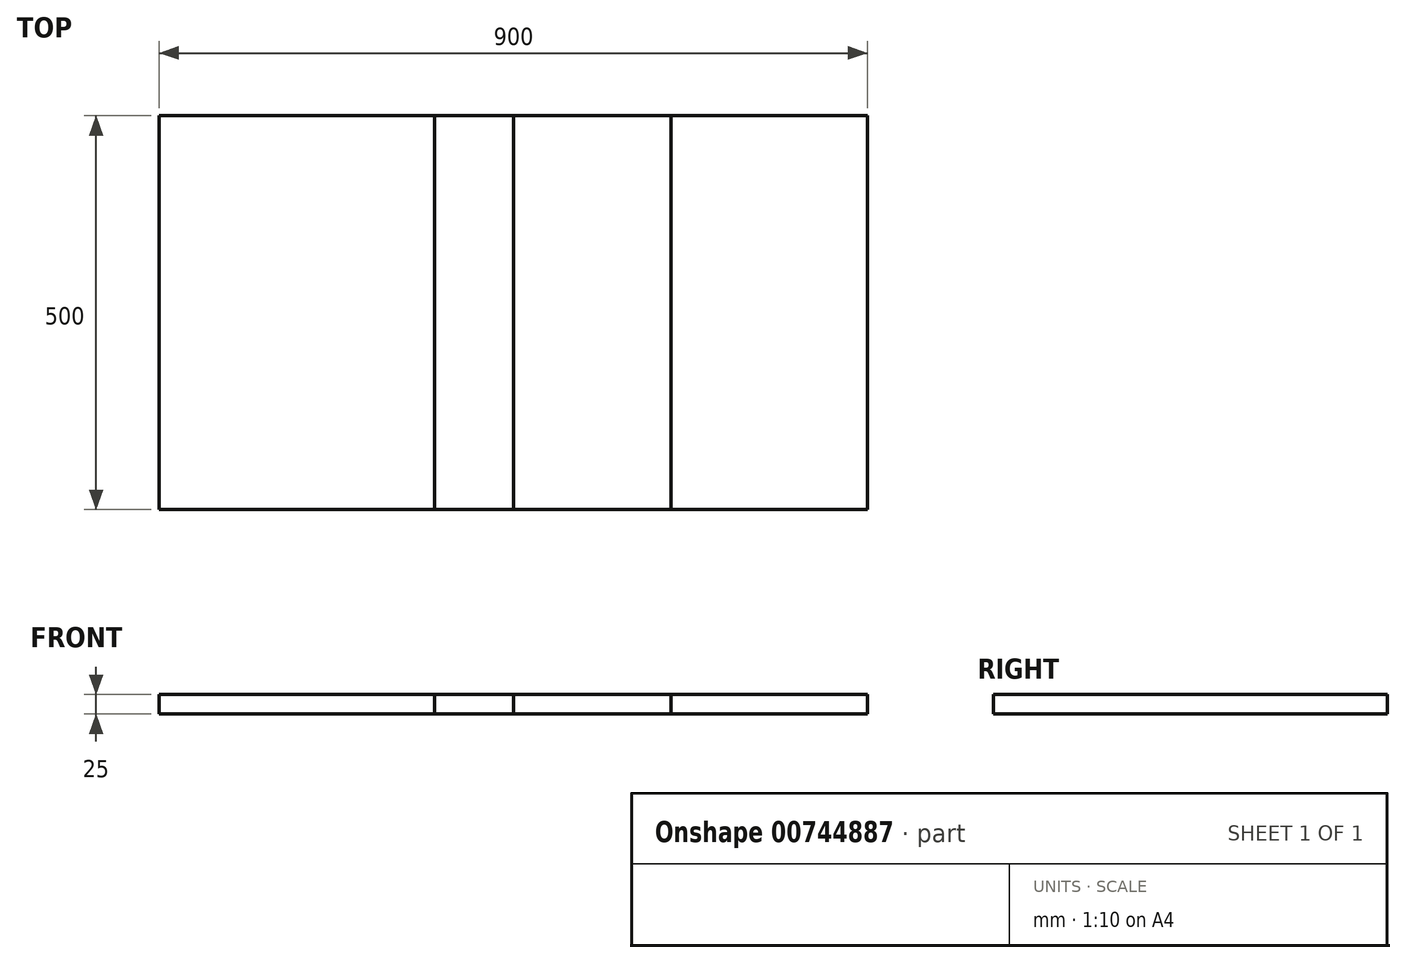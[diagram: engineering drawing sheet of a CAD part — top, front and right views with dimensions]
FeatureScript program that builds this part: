
annotation { "Feature Type Name" : "Feature", "Feature Type Description" : "" }
export const myFeature = defineFeature(function(context is Context, id is Id, definition is map)
    precondition{}
    {
        {
            var Q0;
            Q0=qCreatedBy(makeId("Top.planeOp"),FACE);
            var sketch = newSketch(context, id + "F0", { "sketchPlane" : qUnion([Q0])});
            skLineSegment(sketch, "E0.bottom", {"start": v(-175, 250) * mm, "end": v(175, 250) * mm});
            skLineSegment(sketch, "E0.top", {"start": v(-175, -250) * mm, "end": v(175, -250) * mm});
            skLineSegment(sketch, "E0.left", {"start": v(-175, 250) * mm, "end": v(-175, -250) * mm});
            skLineSegment(sketch, "E0.right", {"start": v(175, 250) * mm, "end": v(175, -250) * mm});
            skPoint(sketch, "E0.middle", {"position": v(0, 0) * mm});
            skSolve(sketch);
        }
        {
            var Q0;
            Q0 = qSketchRegion(id + "F0", true);
            extrude(context, id + "F1", {"entities" : qUnion([Q0]), "depth" : 25 * mm, "offsetDistance" : 25 * mm});
        }
        {
            var Q0;
            Q0=makeQuery(id+"F1.opExtrude","CAP_FACE",FACE,{"disambiguationData":[OSD([sQuery(id+"F0.wireOp",EDGE,"E0.bottom"),sQuery(id+"F0.wireOp",EDGE,"E0.top"),sQuery(id+"F0.wireOp",EDGE,"E0.left"),sQuery(id+"F0.wireOp",EDGE,"E0.right")])],"isStart":true});
            var sketch = newSketch(context, id + "F2", { "sketchPlane" : qUnion([Q0])});
            skLineSegment(sketch, "E1.bottom", {"start": v(175, -250) * mm, "end": v(275, -250) * mm});
            skLineSegment(sketch, "E1.top", {"start": v(175, 250) * mm, "end": v(275, 250) * mm});
            skLineSegment(sketch, "E1.left", {"start": v(175, -250) * mm, "end": v(175, 250) * mm});
            skLineSegment(sketch, "E1.right", {"start": v(275, -250) * mm, "end": v(275, 250) * mm});
            skLineSegment(sketch, "E2.bottom", {"start": v(275, 250) * mm, "end": v(275, 250) * mm});
            skLineSegment(sketch, "E2.top", {"start": v(275, -250) * mm, "end": v(275, -250) * mm});
            skLineSegment(sketch, "E2.left", {"start": v(275, 250) * mm, "end": v(275, -250) * mm});
            skLineSegment(sketch, "E2.right", {"start": v(275, 250) * mm, "end": v(275, -250) * mm});
            skSolve(sketch);
        }
        {
            var Q0;
            Q0 = qSketchRegion(id + "F2", true);
            extrude(context, id + "F3", {"entities" : qUnion([Q0]), "oppositeDirection" : true, "depth" : 25 * mm, "offsetDistance" : 25 * mm});
        }
        {
            var Q0;
            Q0=qCreatedBy(makeId("Top.planeOp"),FACE);
            var sketch = newSketch(context, id + "F4", { "sketchPlane" : qUnion([Q0])});
            skLineSegment(sketch, "E3.bottom", {"start": v(275, -250) * mm, "end": v(475, -250) * mm});
            skLineSegment(sketch, "E3.top", {"start": v(275, 250) * mm, "end": v(475, 250) * mm});
            skLineSegment(sketch, "E3.left", {"start": v(275, -250) * mm, "end": v(275, 250) * mm});
            skLineSegment(sketch, "E3.right", {"start": v(475, -250) * mm, "end": v(475, 250) * mm});
            skSolve(sketch);
        }
        {
            var Q0;
            Q0 = qSketchRegion(id + "F4", true);
            extrude(context, id + "F5", {"entities" : qUnion([Q0]), "depth" : 25 * mm, "offsetDistance" : 25 * mm});
        }
        {
            var Q0;
            Q0=makeQuery(id+"F5.opExtrude","CAP_FACE",FACE,{"disambiguationData":[OSD([sQuery(id+"F4.wireOp",EDGE,"E3.bottom"),sQuery(id+"F4.wireOp",EDGE,"E3.top"),sQuery(id+"F4.wireOp",EDGE,"E3.left"),sQuery(id+"F4.wireOp",EDGE,"E3.right")])],"isStart":true});
            var sketch = newSketch(context, id + "F6", { "sketchPlane" : qUnion([Q0])});
            skLineSegment(sketch, "E4.bottom", {"start": v(475, 250) * mm, "end": v(725, 250) * mm});
            skLineSegment(sketch, "E4.top", {"start": v(475, -250) * mm, "end": v(725, -250) * mm});
            skLineSegment(sketch, "E4.left", {"start": v(475, 250) * mm, "end": v(475, -250) * mm});
            skLineSegment(sketch, "E4.right", {"start": v(725, 250) * mm, "end": v(725, -250) * mm});
            skSolve(sketch);
        }
        {
            var Q0;
            Q0 = qSketchRegion(id + "F6", true);
            extrude(context, id + "F7", {"entities" : qUnion([Q0]), "oppositeDirection" : true, "depth" : 25 * mm, "offsetDistance" : 25 * mm});
        }
    });
